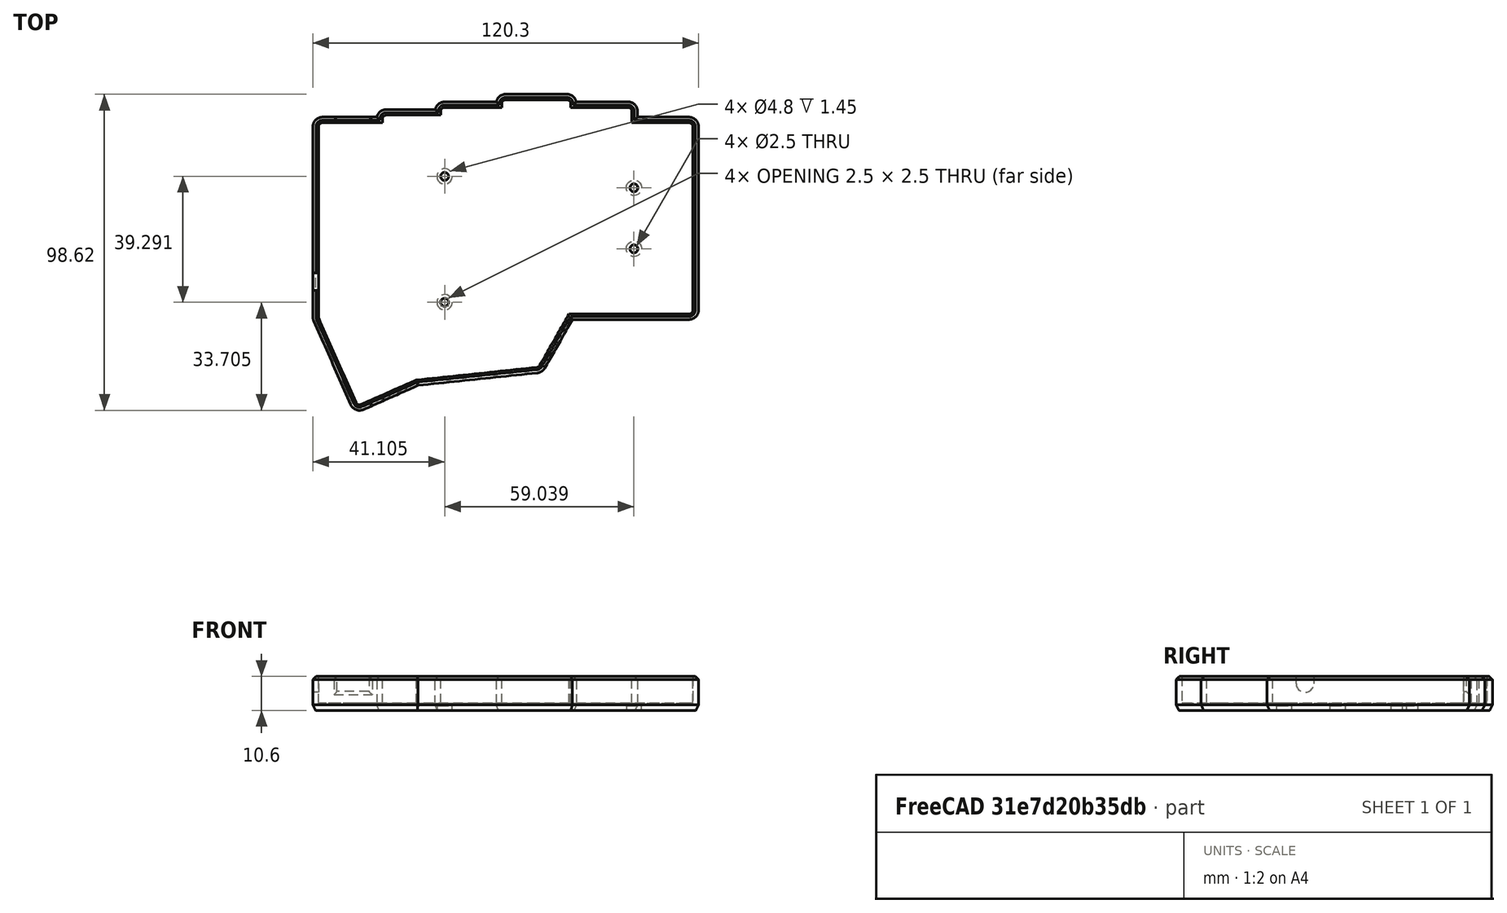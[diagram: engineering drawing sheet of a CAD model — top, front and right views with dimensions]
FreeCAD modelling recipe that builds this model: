
FCSTD DOCUMENT  (FreeCAD 1.0R39109 (Git))
Label: case
License: All rights reserved
LicenseURL: https://en.wikipedia.org/wiki/All_rights_reserved
objects: Part::Feature×1, PartDesign::SubShapeBinder×1, Sketcher::SketchObject×1, PartDesign::Body×1
note: 5 computed .brp shape members not serialized (recipe doc carries the construction recipe); baked Part::Feature solids carry a one-line shape summary decoded from their .brp

FEATURE [Part::Feature] Part__Feature  label="Document"
  Placement = pos=(-59,-315,0) rot=(0,0,1;0rad)
  shape: bbox 120.3 x 99.59 x 10.61 mm, 136 faces (baked)
FEATURE [PartDesign::SubShapeBinder] Binder
  BindCopyOnChange = 0
  BindMode = 0
  ClaimChildren = false
  Context = -> Body [Binder.]
  Fuse = false
  MakeFace = true
  OffsetFill = false
  OffsetIntersection = false
  OffsetJoinType = 0
  OffsetOpenResult = false
  PartialLoad = false
  Refine = true
  Relative = true
  Support = -> [Part__Feature]
  _Version = 2
FEATURE [Sketcher::SketchObject] Sketch
  ArcFitTolerance = 1e-06
  AttachmentSupport = -> [XY_Plane]
  FullyConstrained = false
  MakeInternals = false
  MapMode = 5
  sketch-geometry (23):
    g0: Circle CenterX=46.6149 CenterY=66.2055 CenterZ=0 NormalX=0 NormalY=0 NormalZ=1 AngleXU=0 Radius=1.24999
    g1: Circle CenterX=46.6149 CenterY=26.9148 CenterZ=0 NormalX=0 NormalY=0 NormalZ=1 AngleXU=0 Radius=1.25
    g2: Circle CenterX=105.654 CenterY=43.5837 CenterZ=0 NormalX=0 NormalY=0 NormalZ=1 AngleXU=0 Radius=1.25
    g3: Circle CenterX=105.654 CenterY=62.6336 CenterZ=0 NormalX=0 NormalY=0 NormalZ=1 AngleXU=0 Radius=1.24999
    g4: LineSegment StartX=124.057 StartY=81.6855 StartZ=0 EndX=124.057 EndY=81.6855 EndZ=0
    g5: LineSegment StartX=122.826 StartY=23.2816 StartZ=0 EndX=85.4414 EndY=23.2816 EndZ=0
    g6: LineSegment StartX=76.2764 StartY=7.24284 StartZ=0 EndX=85.4414 EndY=23.2816 EndZ=0
    g7: LineSegment StartX=75.3211 StartY=6.61979 StartZ=0 EndX=37.8285 EndY=2.69899 EndZ=0
    g8: LineSegment StartX=37.7509 StartY=2.66465 StartZ=0 EndX=20.5879 EndY=-4.93393 EndZ=0
    g9: LineSegment StartX=18.9388 StartY=-4.29697 StartZ=0 EndX=7.36988 EndY=21.834 EndZ=0
    g10: LineSegment StartX=7.26287 StartY=22.34 StartZ=0 EndX=7.26287 EndY=81.6856 EndZ=0
    g11: LineSegment StartX=8.51287 StartY=82.9356 StartZ=0 EndX=27.1778 EndY=82.9356 EndZ=0
    g12: LineSegment StartX=27.1778 StartY=84.0669 StartZ=0 EndX=27.1778 EndY=82.9356 EndZ=0
    g13: LineSegment StartX=28.4278 StartY=85.3169 StartZ=0 EndX=45.3629 EndY=85.3169 EndZ=0
    g14: LineSegment StartX=45.3629 StartY=85.3169 StartZ=0 EndX=45.3629 EndY=86.4481 EndZ=0
    g15: LineSegment StartX=46.6129 StartY=87.6981 StartZ=0 EndX=64.4129 EndY=87.6981 EndZ=0
    g16: LineSegment StartX=64.4129 StartY=87.6981 StartZ=0 EndX=64.4129 EndY=88.8294 EndZ=0
    g17: LineSegment StartX=65.6629 StartY=90.0794 StartZ=0 EndX=84.7169 EndY=90.0794 EndZ=0
    g18: LineSegment StartX=85.9669 StartY=88.8294 StartZ=0 EndX=85.9669 EndY=87.6981 EndZ=0
    g19: LineSegment StartX=85.9669 StartY=87.6981 StartZ=0 EndX=103.767 EndY=87.698 EndZ=0
    g20: LineSegment StartX=105.017 StartY=86.448 StartZ=0 EndX=105.017 EndY=82.9356 EndZ=0
    g21: LineSegment StartX=105.017 StartY=82.9356 StartZ=0 EndX=122.807 EndY=82.9355 EndZ=0
    g22: LineSegment StartX=124.057 StartY=81.6855 StartZ=0 EndX=124.057 EndY=24.5316 EndZ=0
  constraints (8):
    c: Vertical(g4)
    c: Horizontal(g5)
    c: Coincident(g6,g5)
    c: Coincident(g12,g11)
    c: Coincident(g14,g13)
    c: Coincident(g16,g15)
    c: Coincident(g19,g18)
    c: Coincident(g21,g20)
FEATURE [PartDesign::Body] Body
  AllowCompound = false
  Group = -> [Binder,Sketch]
  Origin = -> Origin
